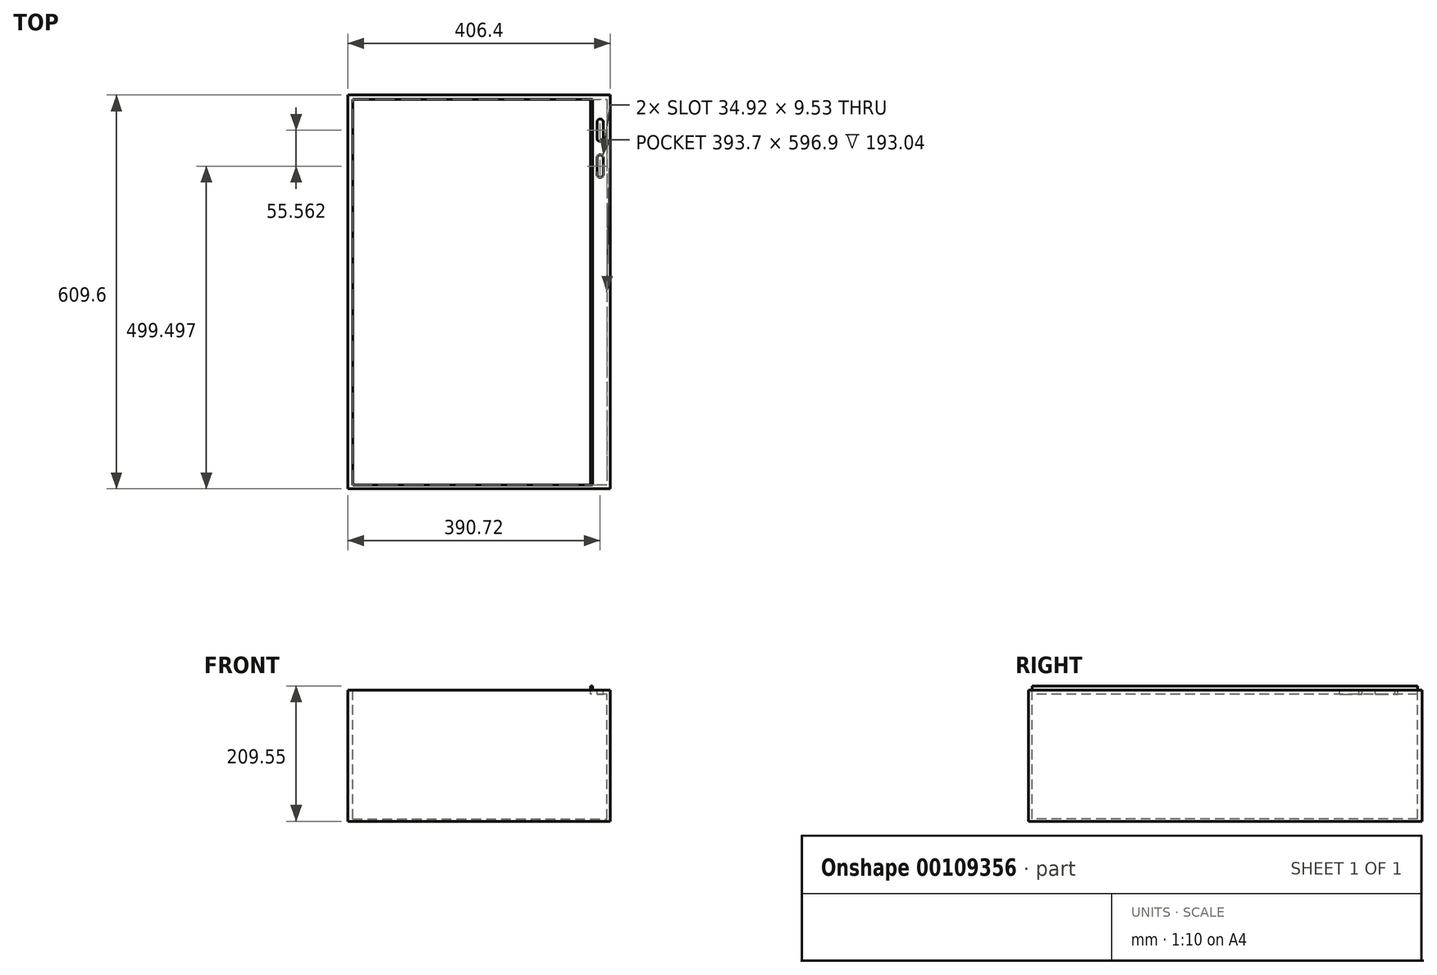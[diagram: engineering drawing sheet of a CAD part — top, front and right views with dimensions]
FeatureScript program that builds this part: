
annotation { "Feature Type Name" : "Feature", "Feature Type Description" : "" }
export const myFeature = defineFeature(function(context is Context, id is Id, definition is map)
    precondition{}
    {
        {
            var Q0;
            Q0=qCreatedBy(makeId("Top.planeOp"),FACE);
            var sketch = newSketch(context, id + "F0", { "sketchPlane" : qUnion([Q0])});
            skLineSegment(sketch, "E0.bottom", {"start": v(-203.2, 304.8) * mm, "end": v(203.2, 304.8) * mm});
            skLineSegment(sketch, "E0.top", {"start": v(-203.2, -304.8) * mm, "end": v(203.2, -304.8) * mm});
            skLineSegment(sketch, "E0.left", {"start": v(-203.2, 304.8) * mm, "end": v(-203.2, -304.8) * mm});
            skLineSegment(sketch, "E0.right", {"start": v(203.2, 304.8) * mm, "end": v(203.2, -304.8) * mm});
            skPoint(sketch, "E0.middle", {"position": v(0, 0) * mm});
            skSolve(sketch);
        }
        {
            var Q0;
            Q0=makeQuery(id+"F0.imprint","IMPRINT",FACE,{"disambiguationData":[TD([[makeQuery(id+"F0.imprint","IMPRINT",EDGE,{"derivedFrom":sQuery(id+"F0.wireOp",EDGE,"E0.bottom")}),-1.0]])]});
            extrude(context, id + "F1", {"entities" : qUnion([Q0]), "depth" : 203.2 * mm});
        }
        {
            var Q0;
            Q0=makeQuery(id+"F1.opExtrude","CAP_FACE",FACE,{"disambiguationData":[OSD([sQuery(id+"F0.wireOp",EDGE,"E0.bottom"),sQuery(id+"F0.wireOp",EDGE,"E0.top"),sQuery(id+"F0.wireOp",EDGE,"E0.left"),sQuery(id+"F0.wireOp",EDGE,"E0.right")])],"isStart":false});
            var sketch = newSketch(context, id + "F2", { "sketchPlane" : qUnion([Q0])});
            skLineSegment(sketch, "E1.bottom", {"start": v(-195.86, 298.13) * mm, "end": v(172.44, 298.13) * mm});
            skLineSegment(sketch, "E1.top", {"start": v(-195.86, -298.77) * mm, "end": v(172.44, -298.77) * mm});
            skLineSegment(sketch, "E1.left", {"start": v(-195.86, 298.13) * mm, "end": v(-195.86, -298.77) * mm});
            skLineSegment(sketch, "E1.right", {"start": v(172.44, 298.13) * mm, "end": v(172.44, -298.77) * mm});
            skSolve(sketch);
        }
        {
            var Q0;
            Q0 = qSketchRegion(id + "F2", true);
            extrude(context, id + "F3", {"entities" : qUnion([Q0]), "operationType" : NewBodyOperationType.REMOVE, "oppositeDirection" : true, "depth" : 199.39 * mm});
        }
        {
            var Q0;
            Q0=makeQuery(id+"F3.boolean.opBoolean","COPY",FACE,{"derivedFrom":makeQuery(id+"F3.opExtrude","SWEPT_FACE",FACE,{"disambiguationData":[OSD([sQuery(id+"F2.wireOp",EDGE,"E1.right")])]})});
            var sketch = newSketch(context, id + "F4", { "sketchPlane" : qUnion([Q0])});
            skLineSegment(sketch, "E2", {"start": v(-77.17, 203.2) * mm, "end": v(-77.17, 196.85) * mm});
            skLineSegment(sketch, "E3.bottom", {"start": v(-298.13, 3.81) * mm, "end": v(298.77, 3.81) * mm});
            skLineSegment(sketch, "E3.top", {"start": v(-298.13, 196.85) * mm, "end": v(298.77, 196.85) * mm});
            skLineSegment(sketch, "E3.left", {"start": v(-298.13, 3.81) * mm, "end": v(-298.13, 196.85) * mm});
            skLineSegment(sketch, "E3.right", {"start": v(298.77, 3.81) * mm, "end": v(298.77, 196.85) * mm});
            skSolve(sketch);
        }
        {
            var Q0;
            Q0 = qSketchRegion(id + "F4", true);
            extrude(context, id + "F5", {"entities" : qUnion([Q0]), "operationType" : NewBodyOperationType.REMOVE, "oppositeDirection" : true, "depth" : 25.4 * mm});
        }
        {
            var Q0;
            Q0=makeQuery(id+"F1.opExtrude","CAP_FACE",FACE,{"disambiguationData":[OSD([sQuery(id+"F0.wireOp",EDGE,"E0.bottom"),sQuery(id+"F0.wireOp",EDGE,"E0.top"),sQuery(id+"F0.wireOp",EDGE,"E0.left"),sQuery(id+"F0.wireOp",EDGE,"E0.right")])],"isStart":false});
            var sketch = newSketch(context, id + "F6", { "sketchPlane" : qUnion([Q0])});
            skArc(sketch, "E4", {"start": v(192.28, 262.87) * mm, "mid": v(187.56, 267.72) * mm, "end": v(182.76, 262.96) * mm});
            skArc(sketch, "E5", {"start": v(182.76, 237.56) * mm, "mid": v(187.52, 232.8) * mm, "end": v(192.28, 237.56) * mm});
            skLineSegment(sketch, "E6", {"start": v(182.76, 262.96) * mm, "end": v(182.76, 237.56) * mm});
            skLineSegment(sketch, "E7", {"start": v(192.28, 262.87) * mm, "end": v(192.28, 237.56) * mm});
            skArc(sketch, "E8", {"start": v(192.28, 207.31) * mm, "mid": v(187.56, 212.16) * mm, "end": v(182.76, 207.4) * mm});
            skArc(sketch, "E9", {"start": v(182.76, 182) * mm, "mid": v(187.52, 177.23) * mm, "end": v(192.28, 182) * mm});
            skLineSegment(sketch, "E10", {"start": v(182.76, 207.4) * mm, "end": v(182.76, 182) * mm});
            skLineSegment(sketch, "E11", {"start": v(192.28, 207.31) * mm, "end": v(192.28, 182) * mm});
            skPoint(sketch, "E12.orphan", {"position": v(187.52, 232.8) * mm});
            skSolve(sketch);
        }
        {
            var Q0;
            Q0=makeQuery(id+"F6.imprint","IMPRINT",FACE,{"disambiguationData":[TD([[makeQuery(id+"F6.imprint","IMPRINT",EDGE,{"derivedFrom":sQuery(id+"F6.wireOp",EDGE,"E4")}),1.0]])]});
            var Q1;
            Q1=makeQuery(id+"F6.imprint","IMPRINT",FACE,{"disambiguationData":[TD([[makeQuery(id+"F6.imprint","IMPRINT",EDGE,{"derivedFrom":sQuery(id+"F6.wireOp",EDGE,"E8")}),1.0]])]});
            extrude(context, id + "F7", {"entities" : qUnion([Q0, Q1]), "operationType" : NewBodyOperationType.REMOVE, "oppositeDirection" : true, "depth" : 25.4 * mm});
        }
        {
            var Q0;
            Q0=makeQuery(id+"F1.opExtrude","CAP_FACE",FACE,{"disambiguationData":[OSD([sQuery(id+"F0.wireOp",EDGE,"E0.bottom"),sQuery(id+"F0.wireOp",EDGE,"E0.top"),sQuery(id+"F0.wireOp",EDGE,"E0.left"),sQuery(id+"F0.wireOp",EDGE,"E0.right")])],"isStart":false});
            var sketch = newSketch(context, id + "F8", { "sketchPlane" : qUnion([Q0])});
            skLineSegment(sketch, "E13", {"start": v(172.44, 298.13) * mm, "end": v(175.61, 298.13) * mm});
            skLineSegment(sketch, "E14", {"start": v(172.44, -298.77) * mm, "end": v(175.61, -298.77) * mm});
            skLineSegment(sketch, "E15", {"start": v(175.61, 298.13) * mm, "end": v(175.61, -298.77) * mm});
            skLineSegment(sketch, "E16", {"start": v(172.44, -298.77) * mm, "end": v(172.44, 298.13) * mm});
            skSolve(sketch);
        }
        {
            var Q0;
            Q0 = qSketchRegion(id + "F8", true);
            extrude(context, id + "F9", {"entities" : qUnion([Q0]), "operationType" : NewBodyOperationType.ADD, "depth" : 6.35 * mm});
        }
    });
